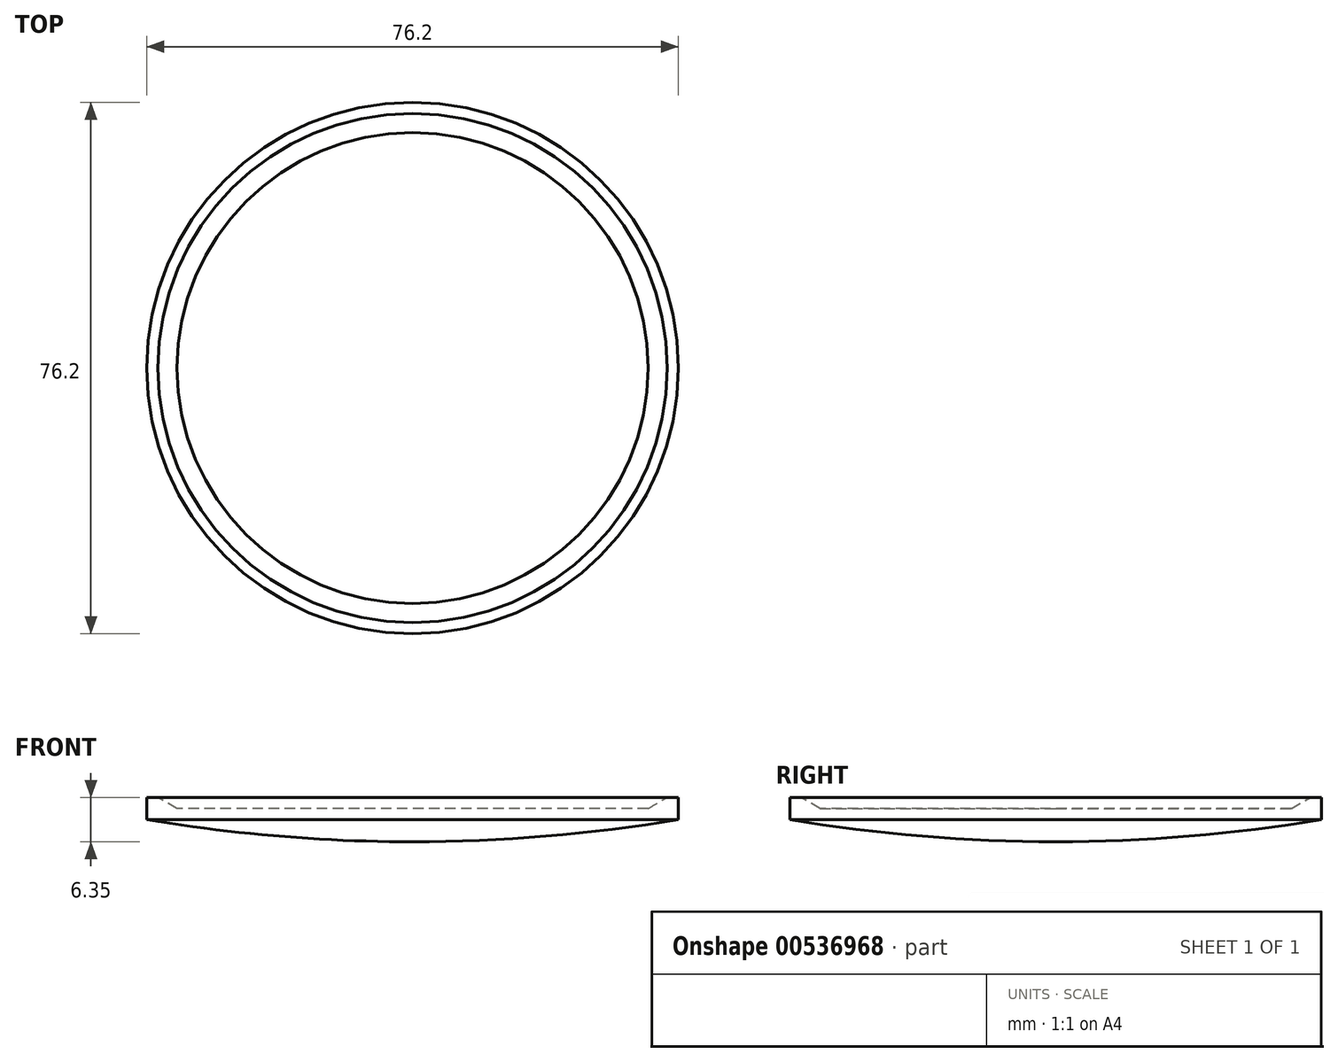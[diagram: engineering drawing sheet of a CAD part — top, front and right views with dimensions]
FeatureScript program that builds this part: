
annotation { "Feature Type Name" : "Feature", "Feature Type Description" : "" }
export const myFeature = defineFeature(function(context is Context, id is Id, definition is map)
    precondition{}
    {
        {
            var Q0;
            Q0=qCreatedBy(makeId("Front.planeOp"),FACE);
            var sketch = newSketch(context, id + "F0", { "sketchPlane" : qUnion([Q0])});
            skLineSegment(sketch, "E0", {"start": v(36.51, 0) * mm, "end": v(38.1, 0) * mm});
            skLineSegment(sketch, "E1", {"start": v(38.1, 0) * mm, "end": v(38.1, -3.18) * mm});
            skLineSegment(sketch, "E2", {"start": v(0, -1.59) * mm, "end": v(0, -6.35) * mm});
            skArc(sketch, "E3", {"start": v(0, -6.35) * mm, "mid": v(19.12, -5.55) * mm, "end": v(38.1, -3.18) * mm});
            skPoint(sketch, "E4.endSnap0", {"position": v(38.1, -1.59) * mm});
            skLineSegment(sketch, "E5", {"start": v(33.76, -1.59) * mm, "end": v(0, -1.59) * mm});
            skLineSegment(sketch, "E6", {"start": v(33.76, -1.59) * mm, "end": v(36.51, 0) * mm});
            skPoint(sketch, "E7.orphan", {"position": v(0, 0) * mm});
            skSolve(sketch);
        }
        {
            var Q0;
            Q0 = qSketchRegion(id + "F0", true);
            var Q1;
            Q1=sQuery(id+"F0.wireOp",EDGE,"E2");
            revolve(context, id + "F1", {"entities" : qUnion([Q0]), "axis" : qUnion([Q1]), "revolveType" : RevolveType.FULL});
        }
    });
